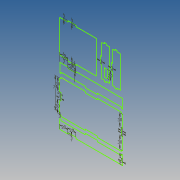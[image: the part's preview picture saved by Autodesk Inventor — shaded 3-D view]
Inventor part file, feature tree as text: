
AUTODESK INVENTOR PART (.ipt)
format: ipt  version: 2020 (Build 240168000, 168)  size: 131,584 bytes
history: native  units: mm
features: sketch x1
ambient origin geometry x8: Origin, YZ Plane, XZ Plane, XY Plane, X Axis, Y Axis, Z Axis, Center Point
feature tree (1):
  sketch  "Sketch1"  dims[d166=74.0mm d174=9.0mm d175=9.0mm d176=3.0mm d182=30.0mm d183=3.0mm d184=30.0mm d185=3.0mm d187=3.0mm d190=3.0mm d192=30.0mm d193=3.0mm d194=30.0mm d195=3.0mm d198=3.0mm d199=20.0mm d200=3.0mm d201=20.0mm d202=20.0mm d203=3.0mm d204=20.0mm d205=3.0mm d206=3.0mm d207=3.0mm d208=3.0mm d210=20.0mm]
